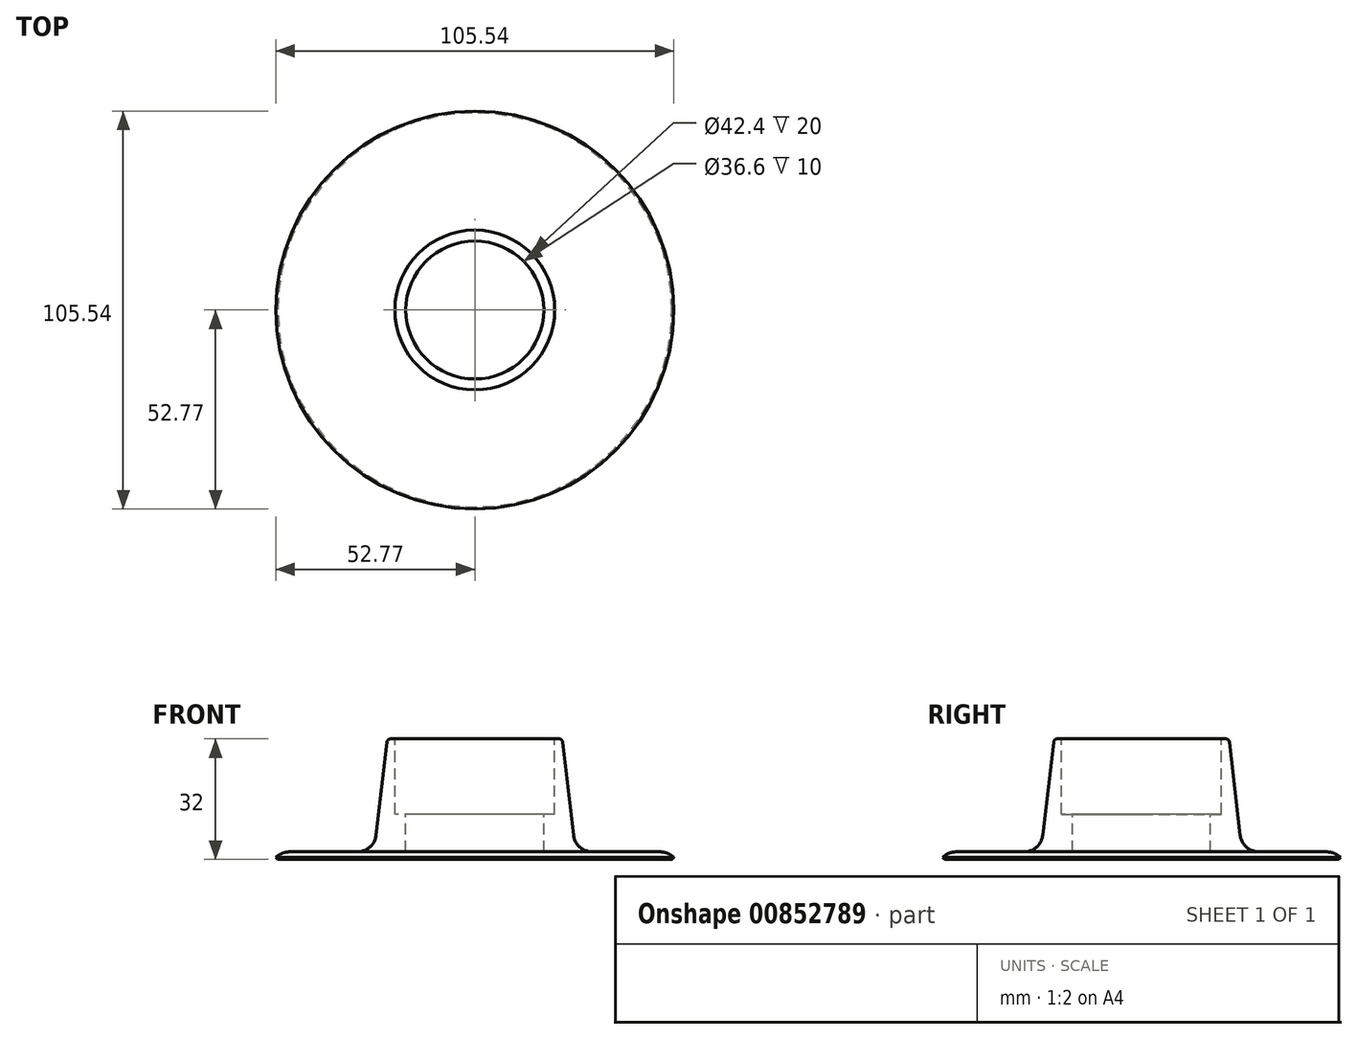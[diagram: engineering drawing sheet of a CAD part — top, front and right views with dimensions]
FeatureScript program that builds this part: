
annotation { "Feature Type Name" : "Feature", "Feature Type Description" : "" }
export const myFeature = defineFeature(function(context is Context, id is Id, definition is map)
    precondition{}
    {
        {
            var Q0;
            Q0=qCreatedBy(makeId("Front.planeOp"),FACE);
            var sketch = newSketch(context, id + "F0", { "sketchPlane" : qUnion([Q0])});
            skLineSegment(sketch, "E0", {"start": v(21.2, 30) * mm, "end": v(21.2, 10) * mm});
            skLineSegment(sketch, "E1", {"start": v(18.3, 0) * mm, "end": v(0, 0) * mm});
            skLineSegment(sketch, "E2", {"start": v(0, 0) * mm, "end": v(0, -2) * mm});
            skLineSegment(sketch, "E3", {"start": v(0, -2) * mm, "end": v(52.77, -2) * mm});
            skLineSegment(sketch, "E4", {"start": v(52.77, -2) * mm, "end": v(52.77, 0) * mm});
            skLineSegment(sketch, "E5", {"start": v(52.77, 0) * mm, "end": v(26.72, 0) * mm});
            skLineSegment(sketch, "E6", {"start": v(21.2, 30) * mm, "end": v(23.2, 30) * mm});
            skLineSegment(sketch, "E7", {"start": v(23.2, 30) * mm, "end": v(26.72, 0) * mm});
            skLineSegment(sketch, "E8", {"start": v(0, 28.48) * mm, "end": v(0, -17.45) * mm, "construction": true});
            skLineSegment(sketch, "E9", {"start": v(21.2, 10) * mm, "end": v(18.3, 10) * mm});
            skLineSegment(sketch, "E10", {"start": v(18.3, 10) * mm, "end": v(18.3, 0) * mm});
            skPoint(sketch, "E11.orphan", {"position": v(21.2, 0) * mm});
            skSolve(sketch);
        }
        {
            var Q0;
            Q0 = qSketchRegion(id + "F0", true);
            var Q1;
            Q1=sQuery(id+"F0.wireOp",EDGE,"E8");
            revolve(context, id + "F1", {"surfaceOperationType" : NewSurfaceOperationType.NEW, "entities" : qUnion([Q0]), "axis" : qUnion([Q1]), "revolveType" : RevolveType.FULL});
        }
        {
            var Q0;
            Q0=makeQuery(id+"F1.opRevolve","SWEPT_FACE",FACE,{"disambiguationData":[OSD([sQuery(id+"F0.wireOp",EDGE,"E3")])]});
            chamfer(context, id + "F2", {"entities" : qUnion([Q0]), "width" : .5 * mm, "tangentPropagation" : true});
        }
        {
            var Q0;
            Q0=makeQuery(id+"F1.opRevolve","SWEPT_FACE",FACE,{"disambiguationData":[OSD([sQuery(id+"F0.wireOp",EDGE,"E5")])]});
            fillet(context, id + "F3", {"entities" : qUnion([Q0]), "radius" : 5 * mm, "tangentPropagation" : true, "allowEdgeOverflow" : false});
        }
        {
            var Q0;
            Q0=makeQuery(id+"F1.opRevolve","SWEPT_EDGE",EDGE,{"disambiguationData":[OSD([sQuery(id+"F0.wireOp",EDGE,"E6"),sQuery(id+"F0.wireOp",EDGE,"E7")])]});
            fillet(context, id + "F4", {"entities" : qUnion([Q0]), "radius" : 1 * mm, "tangentPropagation" : true, "allowEdgeOverflow" : false});
        }
    });
